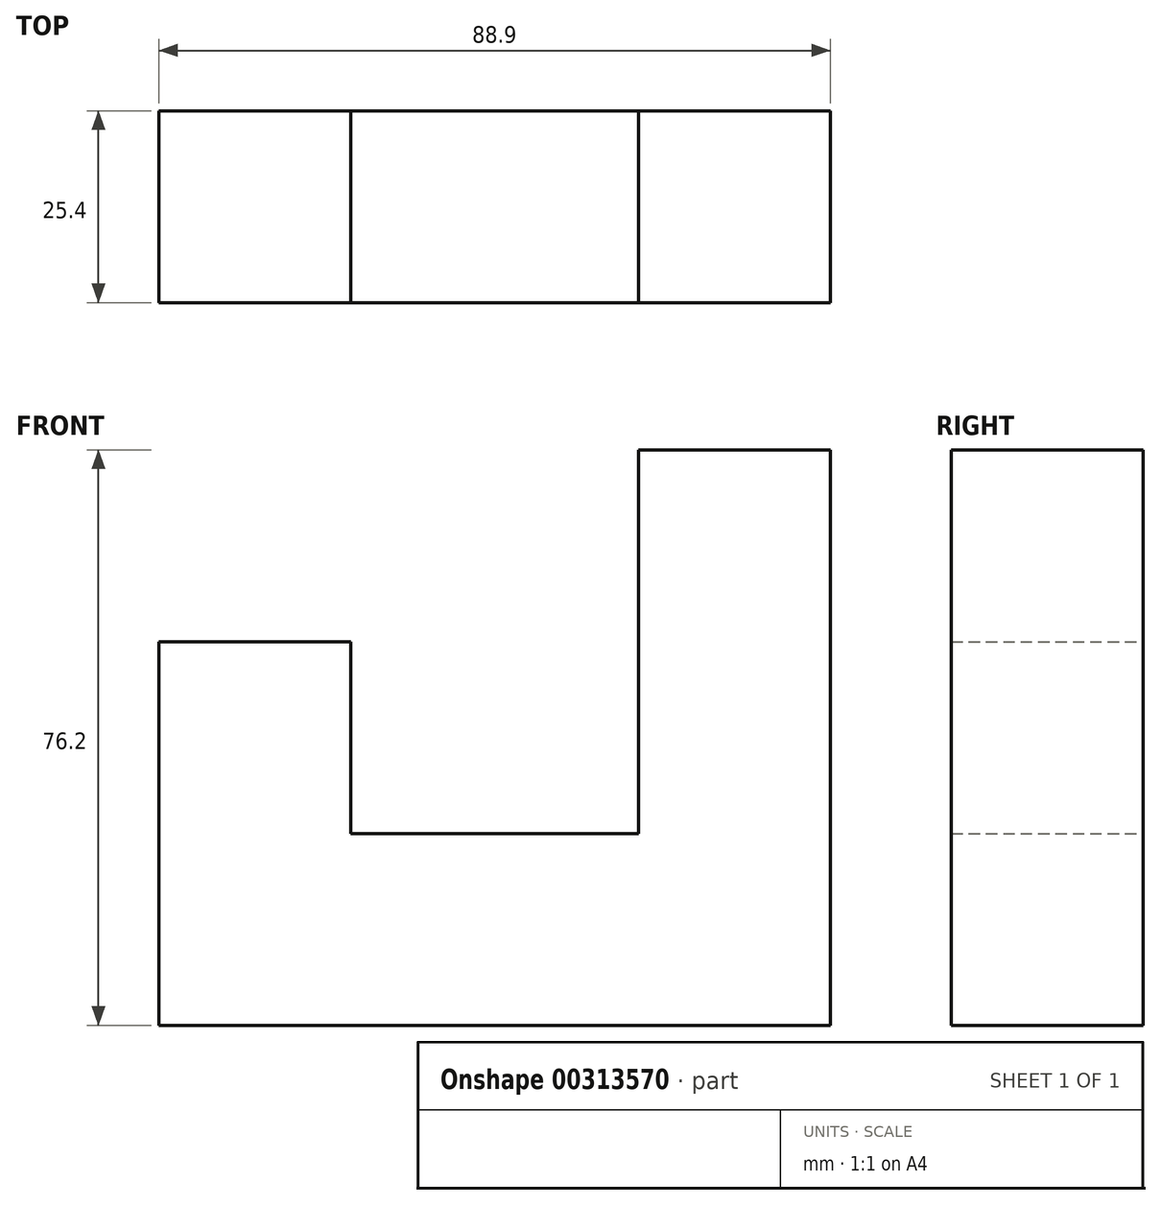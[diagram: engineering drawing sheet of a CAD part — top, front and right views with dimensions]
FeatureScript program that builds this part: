
annotation { "Feature Type Name" : "Feature", "Feature Type Description" : "" }
export const myFeature = defineFeature(function(context is Context, id is Id, definition is map)
    precondition{}
    {
        {
            var Q0;
            Q0=qCreatedBy(makeId("Front.planeOp"),FACE);
            var sketch = newSketch(context, id + "F0", { "sketchPlane" : qUnion([Q0])});
            skLineSegment(sketch, "E0", {"start": v(-44.45, 12.7) * mm, "end": v(-19.05, 12.7) * mm});
            skLineSegment(sketch, "E1", {"start": v(-19.05, 12.7) * mm, "end": v(-19.05, -12.7) * mm});
            skLineSegment(sketch, "E2", {"start": v(-19.05, -12.7) * mm, "end": v(19.05, -12.7) * mm});
            skLineSegment(sketch, "E3", {"start": v(19.05, -12.7) * mm, "end": v(19.05, 38.1) * mm});
            skLineSegment(sketch, "E4", {"start": v(19.05, 38.1) * mm, "end": v(44.45, 38.1) * mm});
            skLineSegment(sketch, "E5", {"start": v(44.45, 38.1) * mm, "end": v(44.45, -38.1) * mm});
            skLineSegment(sketch, "E6", {"start": v(44.45, -38.1) * mm, "end": v(-44.45, -38.1) * mm});
            skLineSegment(sketch, "E7", {"start": v(-44.45, -38.1) * mm, "end": v(-44.45, 12.7) * mm});
            skSolve(sketch);
        }
        {
            var Q0;
            Q0 = qSketchRegion(id + "F0", true);
            extrude(context, id + "F1", {"entities" : qUnion([Q0]), "depth" : 25.4 * mm});
        }
    });
